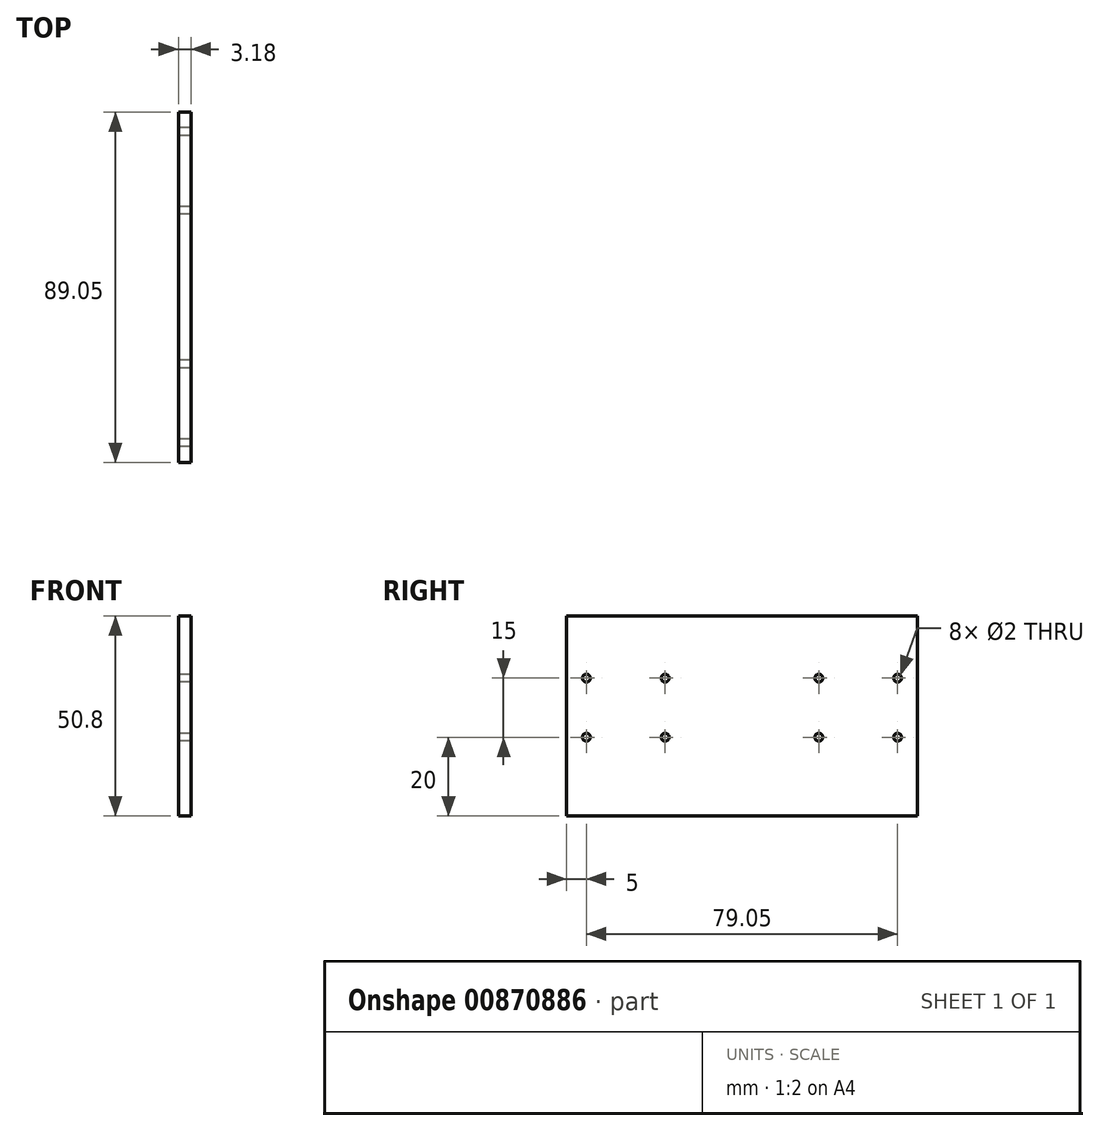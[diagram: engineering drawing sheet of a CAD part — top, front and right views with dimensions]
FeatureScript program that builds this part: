
annotation { "Feature Type Name" : "Feature", "Feature Type Description" : "" }
export const myFeature = defineFeature(function(context is Context, id is Id, definition is map)
    precondition{}
    {
        {
            var Q0;
            Q0=qCreatedBy(makeId("Front.planeOp"),FACE);
            var sketch = newSketch(context, id + "F0", { "sketchPlane" : qUnion([Q0])});
            skLineSegment(sketch, "E0", {"start": v(0, 25.4) * mm, "end": v(0, -25.4) * mm});
            skLineSegment(sketch, "E1", {"start": v(0, -25.4) * mm, "end": v(3.18, -25.4) * mm});
            skLineSegment(sketch, "E2", {"start": v(3.18, -25.4) * mm, "end": v(3.18, 25.4) * mm});
            skLineSegment(sketch, "E3", {"start": v(3.18, 25.4) * mm, "end": v(0, 25.4) * mm});
            skSolve(sketch);
        }
        {
            var Q0;
            Q0 = qSketchRegion(id + "F0", true);
            extrude(context, id + "F1", {"entities" : qUnion([Q0]), "depth" : 89.05 * mm, "offsetDistance" : 25 * mm});
        }
        {
            var Q0;
            Q0=qCreatedBy(makeId("Right.planeOp"),FACE);
            var sketch = newSketch(context, id + "F2", { "sketchPlane" : qUnion([Q0])});
            skPoint(sketch, "E4", {"position": v(-25, 9.6) * mm});
            skPoint(sketch, "E5", {"position": v(-5, 9.6) * mm});
            skPoint(sketch, "E6", {"position": v(-25, -5.4) * mm});
            skPoint(sketch, "E7", {"position": v(-5, -5.4) * mm});
            skPoint(sketch, "E8", {"position": v(-64.05, 9.6) * mm});
            skPoint(sketch, "E9", {"position": v(-84.05, 9.6) * mm});
            skPoint(sketch, "E10", {"position": v(-84.05, -5.4) * mm});
            skPoint(sketch, "E11", {"position": v(-64.05, -5.4) * mm});
            skCircle(sketch, "E12", {"center": v(-84.05, 9.6) * mm, "radius": 1 * mm});
            skCircle(sketch, "E13", {"center": v(-64.05, 9.6) * mm, "radius": 1 * mm});
            skCircle(sketch, "E14", {"center": v(-64.05, -5.4) * mm, "radius": 1 * mm});
            skCircle(sketch, "E15", {"center": v(-84.05, -5.4) * mm, "radius": 1 * mm});
            skCircle(sketch, "E16", {"center": v(-25, -5.4) * mm, "radius": 1 * mm});
            skCircle(sketch, "E17", {"center": v(-25, 9.6) * mm, "radius": 1 * mm});
            skCircle(sketch, "E18", {"center": v(-5, -5.4) * mm, "radius": 1 * mm});
            skCircle(sketch, "E19", {"center": v(-5, 9.6) * mm, "radius": 1 * mm});
            skSolve(sketch);
        }
        {
            var Q0;
            Q0 = qSketchRegion(id + "F2", true);
            extrude(context, id + "F3", {"entities" : qUnion([Q0]), "operationType" : NewBodyOperationType.REMOVE, "endBound" : BoundingType.THROUGH_ALL, "depth" : 25 * mm, "offsetDistance" : 25 * mm});
        }
    });
